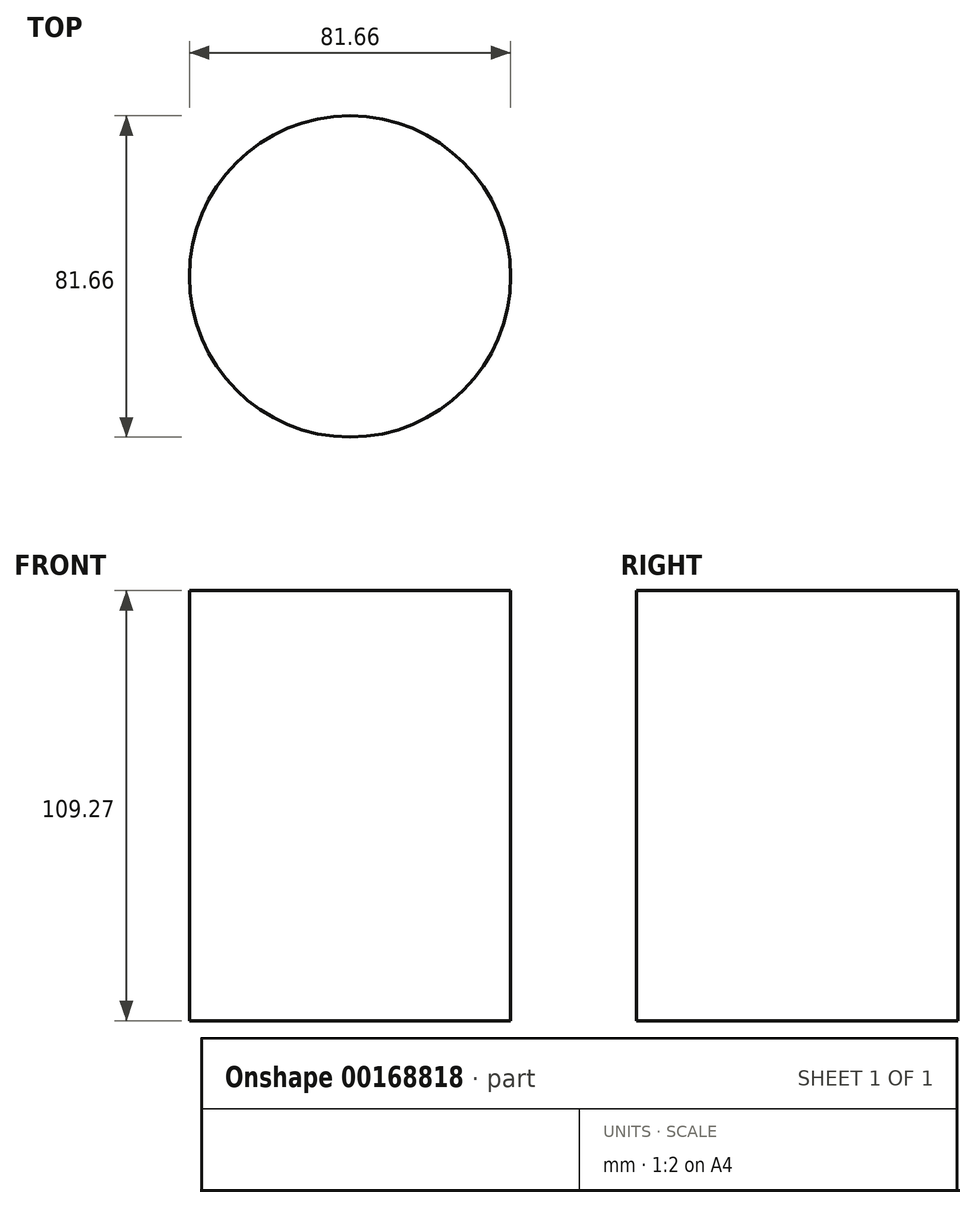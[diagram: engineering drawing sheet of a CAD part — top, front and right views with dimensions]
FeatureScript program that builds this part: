
annotation { "Feature Type Name" : "Feature", "Feature Type Description" : "" }
export const myFeature = defineFeature(function(context is Context, id is Id, definition is map)
    precondition{}
    {
        {
            var Q0;
            Q0=qCreatedBy(makeId("Top.planeOp"),FACE);
            var sketch = newSketch(context, id + "F4", { "sketchPlane" : qUnion([Q0])});
            skCircle(sketch, "E0", {"center": v(0, 0) * mm, "radius": 40.83 * mm});
            skSolve(sketch);
        }
        {
            var Q0;
            Q0 = qSketchRegion(id + "F4", true);
            extrude(context, id + "F0", {"entities" : qUnion([Q0]), "depth" : 109.27 * mm});
        }
    });
